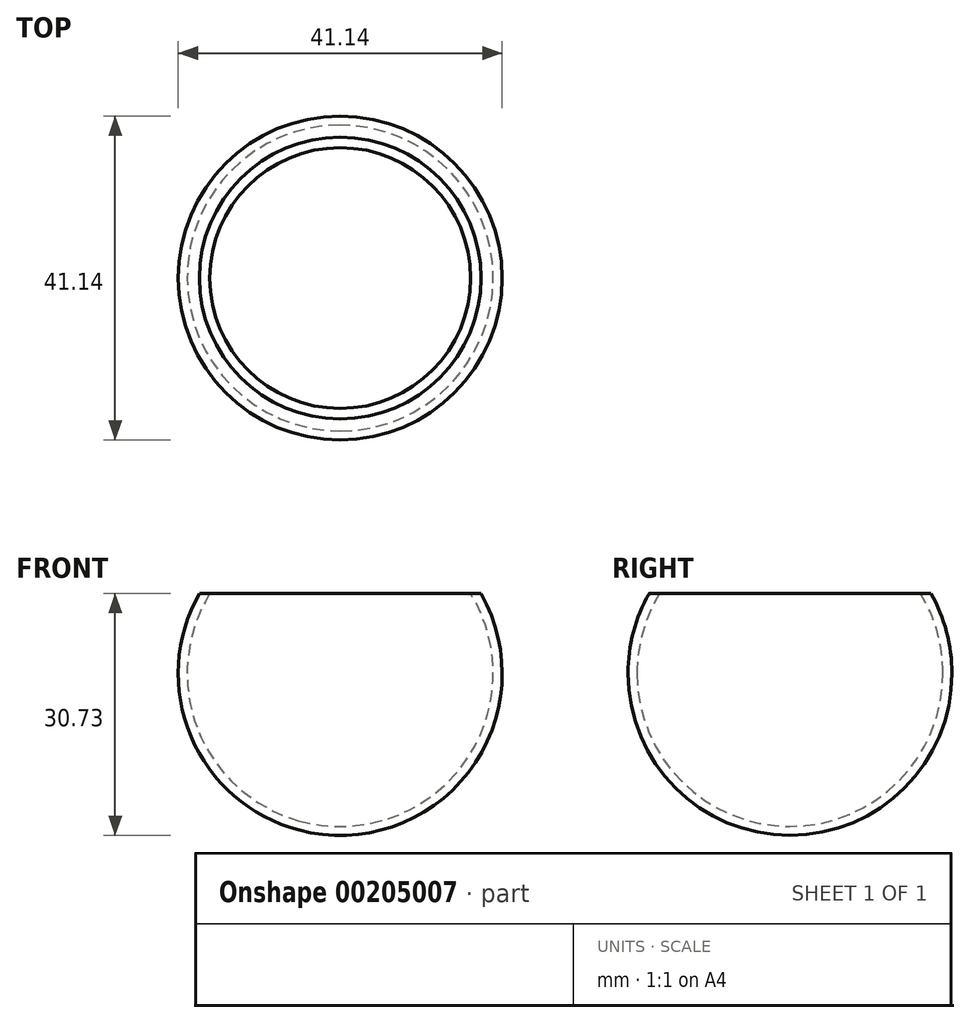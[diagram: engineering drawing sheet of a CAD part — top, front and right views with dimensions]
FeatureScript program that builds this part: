
annotation { "Feature Type Name" : "Feature", "Feature Type Description" : "" }
export const myFeature = defineFeature(function(context is Context, id is Id, definition is map)
    precondition{}
    {
        {
            var Q0;
            Q0=qCreatedBy(makeId("Top.planeOp"),FACE);
            var sketch = newSketch(context, id + "F0", { "sketchPlane" : qUnion([Q0])});
            skCircle(sketch, "E0", {"center": v(0, 0) * mm, "radius": 20.57 * mm});
            skCircle(sketch, "E1", {"center": v(0, 0) * mm, "radius": 19.43 * mm});
            skLineSegment(sketch, "E2", {"start": v(0, 0) * mm, "end": v(0, 20.57) * mm});
            skLineSegment(sketch, "E3", {"start": v(0, 20.57) * mm, "end": v(0, -20.57) * mm});
            skSolve(sketch);
        }
        {
            var Q0;
            {var subQ0=sQuery(id+"F0.wireOp",EDGE,"E3");var subQ1=sQuery(id+"F0.wireOp",EDGE,"E0");var subQ2=makeQuery(id+"F0.imprint","INTERSECT",VERTEX,{"disambiguationData":[OD(0.0)],"derivedFrom":[subQ1,subQ0]});Q0=makeQuery(id+"F0.imprint","IMPRINT",FACE,{"disambiguationData":[TD([[makeQuery(id+"F0.imprint","IMPRINT",EDGE,{"disambiguationData":[TD([[subQ2,1.0]])],"derivedFrom":subQ1}),1.0]])]});}
            var Q1;
            Q1=sQuery(id+"F0.wireOp",EDGE,"E3");
            revolve(context, id + "F1", {"entities" : qUnion([Q0]), "axis" : qUnion([Q1]), "revolveType" : RevolveType.FULL});
        }
        {
            var Q0;
            Q0=qCreatedBy(makeId("Top.planeOp"),FACE);
            cPlane(context, id + "F2", {"entities" : qUnion([Q0]), "cplaneType" : CPlaneType.OFFSET, "offset" : 10.16 * mm, "width" : 152.4 * mm, "height" : 152.4 * mm});
        }
        {
            var Q0;
            Q0=qCreatedBy(id+"F2.planeOp",FACE);
            var sketch = newSketch(context, id + "F3", { "sketchPlane" : qUnion([Q0])});
            skCircle(sketch, "E4", {"center": v(0, 0) * mm, "radius": 20.57 * mm});
            skSolve(sketch);
        }
        {
            var Q0;
            Q0 = qSketchRegion(id + "F3", true);
            extrude(context, id + "F4", {"entities" : qUnion([Q0]), "operationType" : NewBodyOperationType.REMOVE, "endBound" : BoundingType.THROUGH_ALL, "depth" : 25.4 * mm});
        }
    });
